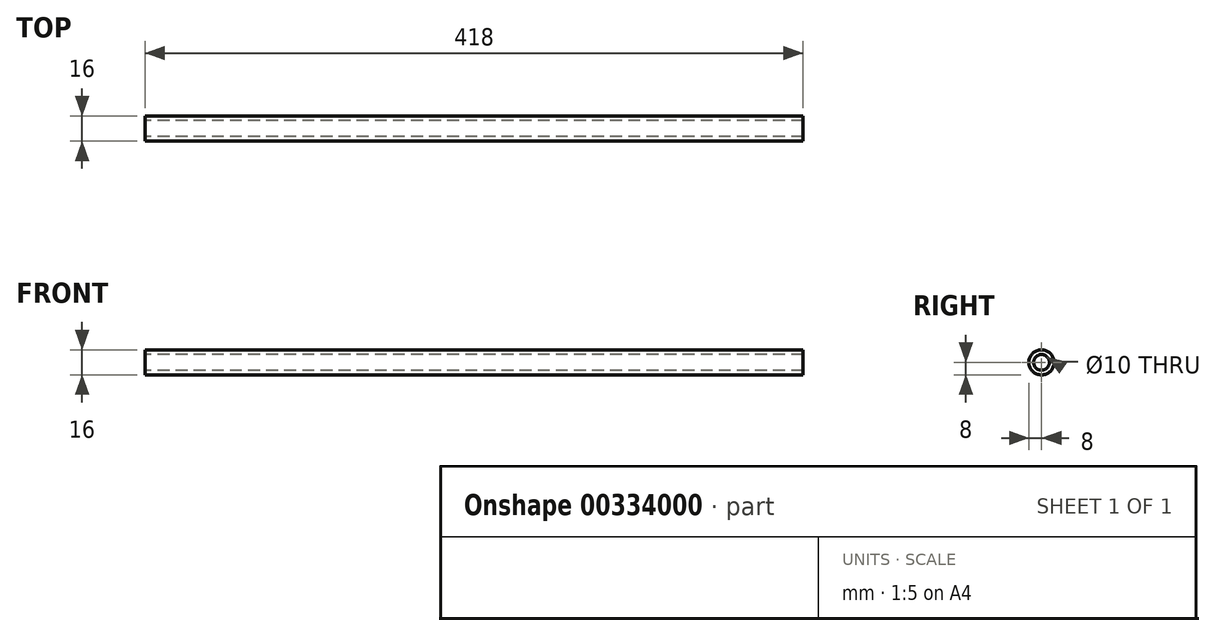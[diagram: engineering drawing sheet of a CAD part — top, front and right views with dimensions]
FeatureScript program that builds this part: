
annotation { "Feature Type Name" : "Feature", "Feature Type Description" : "" }
export const myFeature = defineFeature(function(context is Context, id is Id, definition is map)
    precondition{}
    {
        {
            var Q0;
            Q0=qCreatedBy(makeId("Right.planeOp"),FACE);
            var sketch = newSketch(context, id + "F0", { "sketchPlane" : qUnion([Q0])});
            skCircle(sketch, "E0", {"center": v(0, 0) * mm, "radius": 8 * mm});
            skCircle(sketch, "E1", {"center": v(0, 0) * mm, "radius": 5 * mm});
            skSolve(sketch);
        }
        {
            var Q0;
            Q0=makeQuery(id+"F0.imprint","IMPRINT",FACE,{"disambiguationData":[TD([[makeQuery(id+"F0.imprint","IMPRINT",EDGE,{"derivedFrom":sQuery(id+"F0.wireOp",EDGE,"E0")}),1.0]])]});
            extrude(context, id + "F1", {"entities" : qUnion([Q0]), "depth" : 418 * mm});
        }
    });
